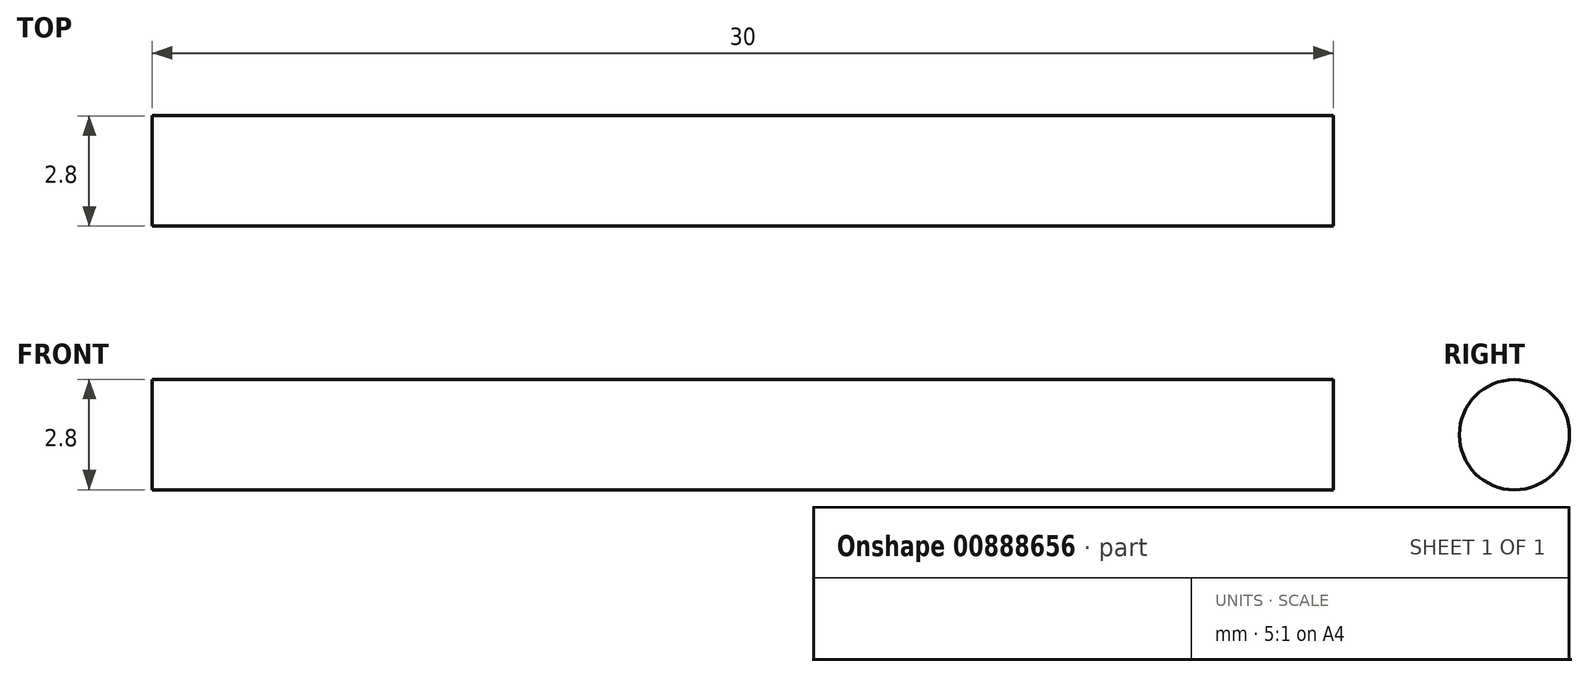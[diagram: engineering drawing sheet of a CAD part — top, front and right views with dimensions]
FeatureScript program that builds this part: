
annotation { "Feature Type Name" : "Feature", "Feature Type Description" : "" }
export const myFeature = defineFeature(function(context is Context, id is Id, definition is map)
    precondition{}
    {
        {
            var Q0;
            Q0=qCreatedBy(makeId("Right.planeOp"),FACE);
            var sketch = newSketch(context, id + "F0", { "sketchPlane" : qUnion([Q0])});
            skCircle(sketch, "E0", {"center": v(-7.79, 4.66) * mm, "radius": 1.4 * mm});
            skSolve(sketch);
        }
        {
            var Q0;
            Q0 = qSketchRegion(id + "F0", true);
            extrude(context, id + "F1", {"entities" : qUnion([Q0]), "depth" : 30 * mm, "offsetDistance" : 25 * mm});
        }
    });
